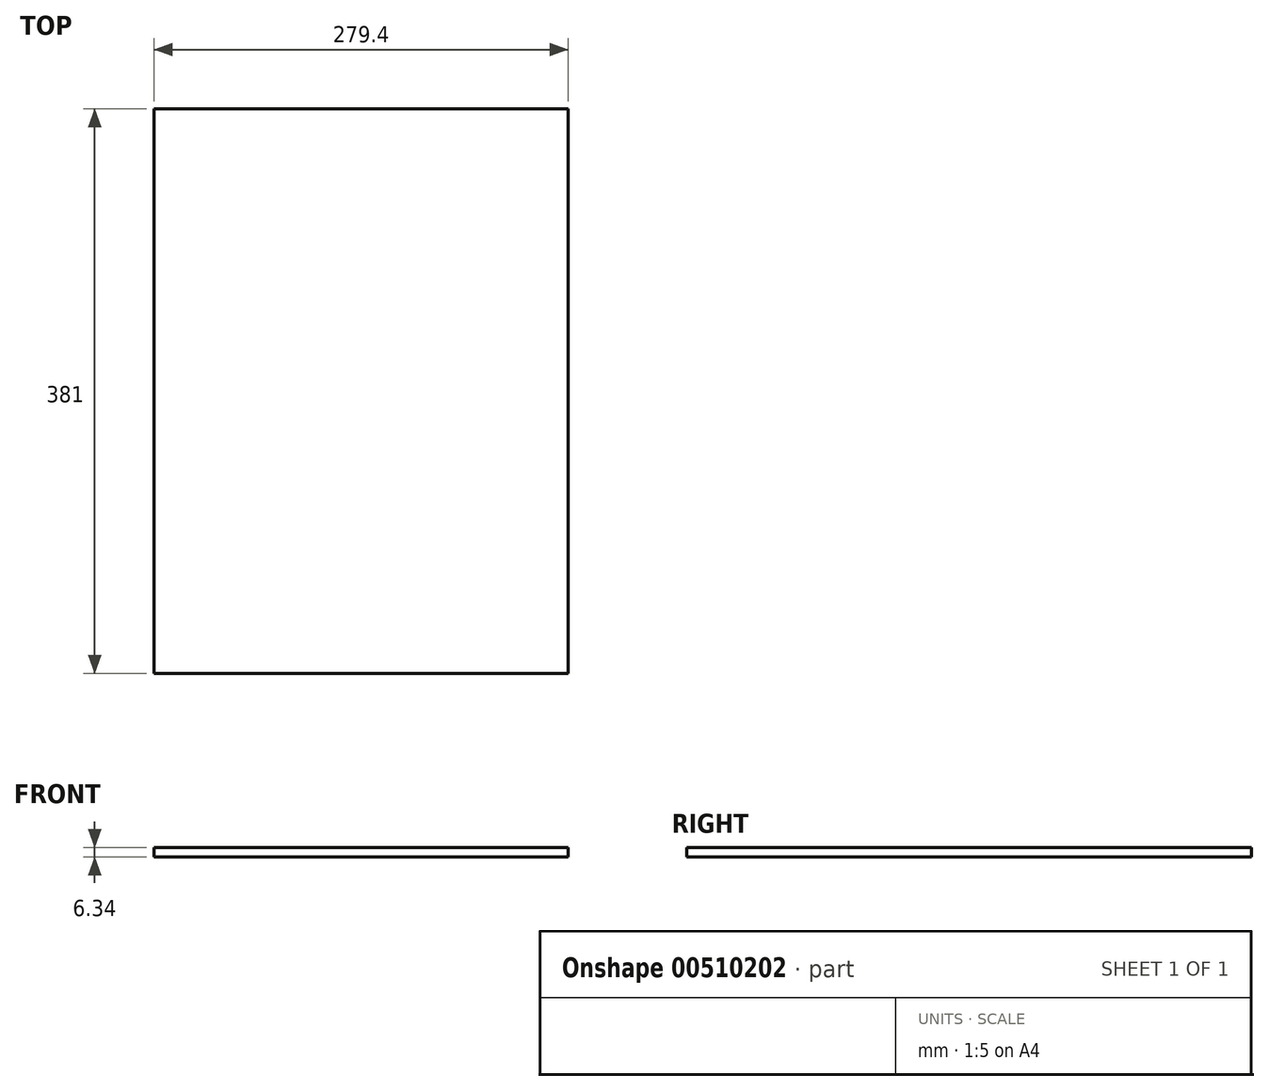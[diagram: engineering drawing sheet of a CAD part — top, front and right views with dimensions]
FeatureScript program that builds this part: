
annotation { "Feature Type Name" : "Feature", "Feature Type Description" : "" }
export const myFeature = defineFeature(function(context is Context, id is Id, definition is map)
    precondition{}
    {
        {
            var Q0;
            Q0=qCreatedBy(makeId("Top.planeOp"),FACE);
            var sketch = newSketch(context, id + "F0", { "sketchPlane" : qUnion([Q0])});
            skLineSegment(sketch, "E0.bottom", {"start": v(139.7, -190.5) * mm, "end": v(-139.7, -190.5) * mm});
            skLineSegment(sketch, "E0.top", {"start": v(139.7, 190.5) * mm, "end": v(-139.7, 190.5) * mm});
            skLineSegment(sketch, "E0.left", {"start": v(139.7, -190.5) * mm, "end": v(139.7, 190.5) * mm});
            skLineSegment(sketch, "E0.right", {"start": v(-139.7, -190.5) * mm, "end": v(-139.7, 190.5) * mm});
            skPoint(sketch, "E0.middle", {"position": v(0, 0) * mm});
            skSolve(sketch);
        }
        {
            var Q0;
            Q0=makeQuery(id+"F0.imprint","IMPRINT",FACE,{"disambiguationData":[TD([[makeQuery(id+"F0.imprint","IMPRINT",EDGE,{"derivedFrom":sQuery(id+"F0.wireOp",EDGE,"E0.bottom")}),-1.0]])]});
            extrude(context, id + "F1", {"entities" : qUnion([Q0]), "endBound" : BoundingType.SYMMETRIC, "depth" : 6.35 * mm});
        }
    });
